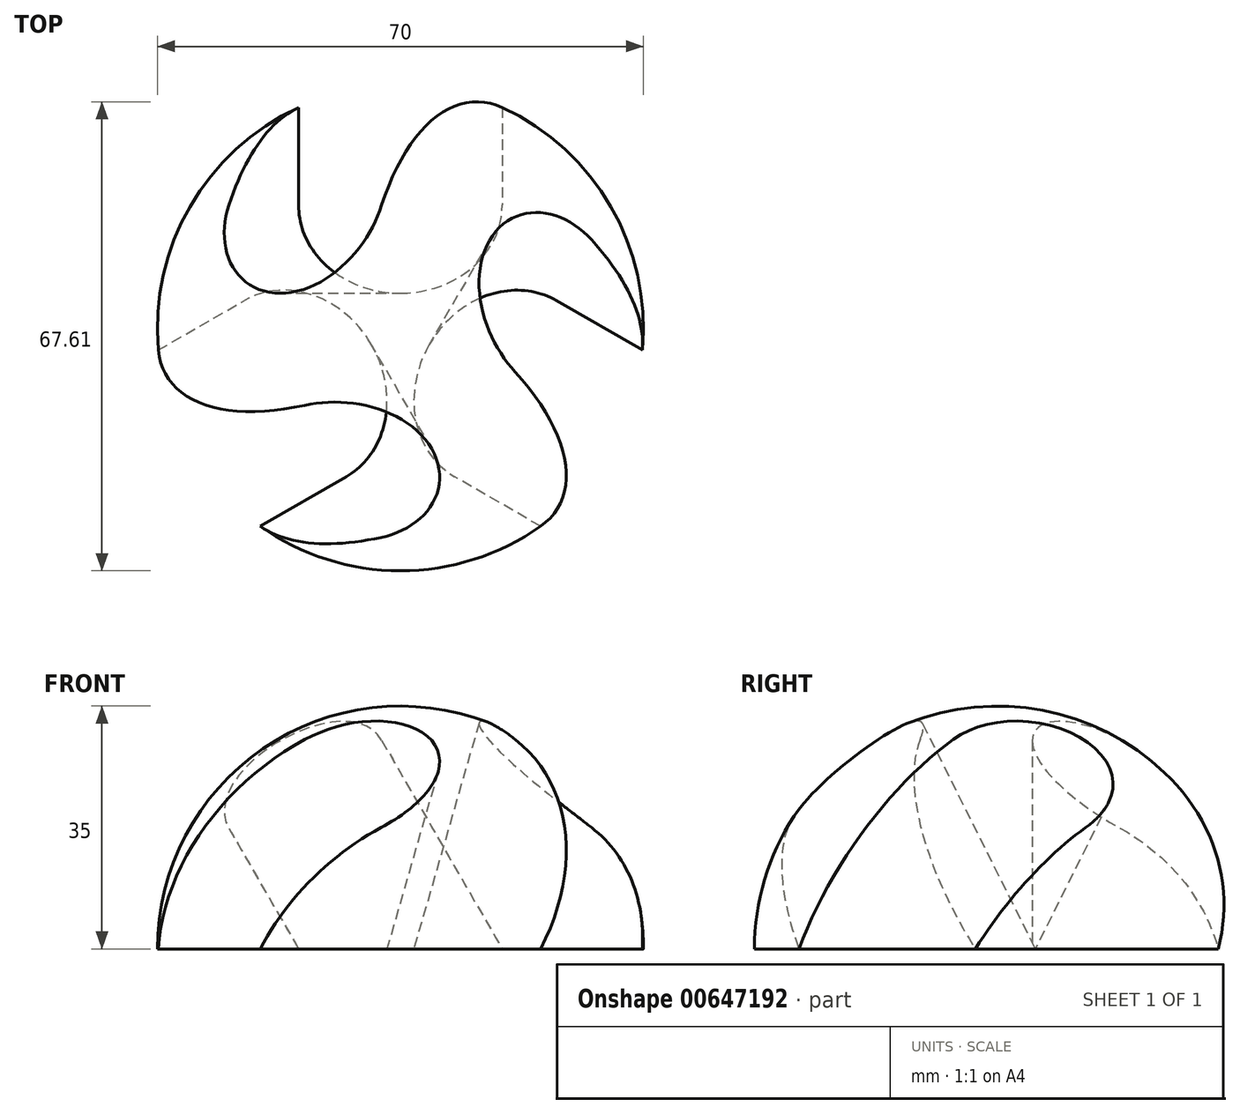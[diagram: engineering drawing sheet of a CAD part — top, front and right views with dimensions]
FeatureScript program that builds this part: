
annotation { "Feature Type Name" : "Feature", "Feature Type Description" : "" }
export const myFeature = defineFeature(function(context is Context, id is Id, definition is map)
    precondition{}
    {
        {
            var Q0;
            Q0=qCreatedBy(makeId("Top.planeOp"),FACE);
            var sketch = newSketch(context, id + "F0", { "sketchPlane" : qUnion([Q0])});
            skArc(sketch, "E0", {"start": v(0, -35) * mm, "mid": v(35, 0) * mm, "end": v(0, 35) * mm});
            skLineSegment(sketch, "E1", {"start": v(0, 35) * mm, "end": v(0, -35) * mm});
            skSolve(sketch);
        }
        {
            var Q0;
            Q0=qCreatedBy(makeId("Top.planeOp"),FACE);
            var sketch = newSketch(context, id + "F1", { "sketchPlane" : qUnion([Q0])});
            skLineSegment(sketch, "E2", {"start": v(0, 18.5) * mm, "end": v(0, -17.36) * mm, "construction": true});
            skSolve(sketch);
        }
        {
            var Q0;
            Q0 = qSketchRegion(id + "F0", true);
            var Q1;
            Q1=sQuery(id+"F0.wireOp",EDGE,"E1");
            revolve(context, id + "F2", {"entities" : qUnion([Q0]), "axis" : qUnion([Q1]), "revolveType" : RevolveType.FULL});
        }
        {
            var Q0;
            Q0=qCreatedBy(makeId("Front.planeOp"),FACE);
            var sketch = newSketch(context, id + "F3", { "sketchPlane" : qUnion([Q0])});
            skLineSegment(sketch, "E3.bottom", {"start": v(56.38, 0) * mm, "end": v(-54.62, 0) * mm});
            skLineSegment(sketch, "E3.top", {"start": v(56.38, -44.46) * mm, "end": v(-54.62, -44.46) * mm});
            skLineSegment(sketch, "E3.left", {"start": v(56.38, 0) * mm, "end": v(56.38, -44.46) * mm});
            skLineSegment(sketch, "E3.right", {"start": v(-54.62, 0) * mm, "end": v(-54.62, -44.46) * mm});
            skSolve(sketch);
        }
        {
            var Q0;
            Q0 = qSketchRegion(id + "F3", true);
            extrude(context, id + "F4", {"entities" : qUnion([Q0]), "operationType" : NewBodyOperationType.REMOVE, "oppositeDirection" : true, "depth" : 40 * mm, "offsetDistance" : 25 * mm, "hasSecondDirection" : true, "secondDirectionOppositeDirection" : false, "secondDirectionDepth" : 40 * mm});
        }
        {
            var Q0;
            Q0=qCreatedBy(makeId("Top.planeOp"),FACE);
            var Q1;
            Q1=sQuery(id+"F1.wireOp",EDGE,"E2");
            cPlane(context, id + "F5", {"entities" : qUnion([Q0, Q1]), "cplaneType" : CPlaneType.LINE_ANGLE, "offset" : 25 * mm, "angle" : 30 * degree, "width" : 150 * mm, "height" : 150 * mm});
        }
        {
            var Q0;
            Q0=qCreatedBy(id+"F5.planeOp",FACE);
            var sketch = newSketch(context, id + "F6", { "sketchPlane" : qUnion([Q0])});
            skArc(sketch, "E4", {"start": v(12.7, -17.72) * mm, "mid": v(0, -5.02) * mm, "end": v(-12.7, -17.72) * mm});
            skLineSegment(sketch, "E5.0", {"start": v(-12.7, -17.72) * mm, "end": v(-12.7, -40.82) * mm});
            skLineSegment(sketch, "E6.0", {"start": v(12.7, -17.72) * mm, "end": v(12.7, -40.82) * mm});
            skLineSegment(sketch, "E7.0", {"start": v(12.7, -40.82) * mm, "end": v(-12.7, -40.82) * mm});
            skSolve(sketch);
        }
        {
            var Q0;
            Q0 = qSketchRegion(id + "F6", true);
            extrude(context, id + "F7", {"entities" : qUnion([Q0]), "operationType" : NewBodyOperationType.REMOVE, "oppositeDirection" : true, "depth" : 60 * mm, "offsetDistance" : 25 * mm, "hasSecondDirection" : true, "secondDirectionOppositeDirection" : false, "secondDirectionDepth" : 25 * mm});
        }
        {
            var Q0;
            Q0=qCreatedBy(makeId("Top.planeOp"),FACE);
            var sketch = newSketch(context, id + "F8", { "sketchPlane" : qUnion([Q0])});
            skLineSegment(sketch, "E8", {"start": v(0, 0) * mm, "end": v(0, 44.27) * mm});
            skLineSegment(sketch, "E9", {"start": v(0, 0) * mm, "end": v(-30.31, -17.5) * mm});
            skLineSegment(sketch, "E10", {"start": v(0, 0) * mm, "end": v(30.31, -17.5) * mm});
            skArc(sketch, "E11.0", {"start": v(-14.66, 31.78) * mm, "mid": v(0, -35) * mm, "end": v(14.66, 31.78) * mm});
            skSolve(sketch);
        }
        {
            var Q0;
            Q0=qCreatedBy(makeId("Top.planeOp"),FACE);
            var sketch = newSketch(context, id + "F9", { "sketchPlane" : qUnion([Q0])});
            skLineSegment(sketch, "E12", {"start": v(0, 0) * mm, "end": v(-65.85, -38.02) * mm, "construction": true});
            skSolve(sketch);
        }
        {
            var Q0;
            Q0=qCreatedBy(makeId("Top.planeOp"),FACE);
            var Q1;
            Q1=sQuery(id+"F9.wireOp",EDGE,"E12");
            cPlane(context, id + "F10", {"entities" : qUnion([Q0, Q1]), "cplaneType" : CPlaneType.LINE_ANGLE, "offset" : 25 * mm, "angle" : 30 * degree, "oppositeDirection" : true, "width" : 150 * mm, "height" : 150 * mm});
        }
        {
            var Q0;
            Q0=qCreatedBy(id+"F10.planeOp",FACE);
            var sketch = newSketch(context, id + "F11", { "sketchPlane" : qUnion([Q0])});
            skArc(sketch, "E13", {"start": v(-21.33, -3.53) * mm, "mid": v(-4.3, 2.15) * mm, "end": v(-9.97, 19.19) * mm});
            skLineSegment(sketch, "E14.0", {"start": v(-9.97, 19.19) * mm, "end": v(-25.63, 27.01) * mm});
            skLineSegment(sketch, "E15.0", {"start": v(-21.33, -3.53) * mm, "end": v(-36.98, 4.3) * mm});
            skLineSegment(sketch, "E16", {"start": v(-25.63, 27.01) * mm, "end": v(-36.98, 4.3) * mm});
            skSolve(sketch);
        }
        {
            var Q0;
            Q0 = qSketchRegion(id + "F11", true);
            extrude(context, id + "F12", {"entities" : qUnion([Q0]), "operationType" : NewBodyOperationType.REMOVE, "oppositeDirection" : true, "depth" : 60 * mm, "offsetDistance" : 25 * mm, "hasSecondDirection" : true, "secondDirectionOppositeDirection" : false, "secondDirectionDepth" : 60 * mm});
        }
        {
            var Q0;
            Q0=qCreatedBy(makeId("Top.planeOp"),FACE);
            var sketch = newSketch(context, id + "F13", { "sketchPlane" : qUnion([Q0])});
            skLineSegment(sketch, "E17", {"start": v(0, 0) * mm, "end": v(53.93, -31.14) * mm, "construction": true});
            skSolve(sketch);
        }
        {
            var Q0;
            Q0=qCreatedBy(makeId("Top.planeOp"),FACE);
            var Q1;
            Q1=sQuery(id+"F13.wireOp",EDGE,"E17");
            cPlane(context, id + "F14", {"entities" : qUnion([Q0, Q1]), "cplaneType" : CPlaneType.LINE_ANGLE, "offset" : 25 * mm, "angle" : 30 * degree, "oppositeDirection" : true, "width" : 150 * mm, "height" : 150 * mm});
        }
        {
            var Q0;
            Q0=qCreatedBy(id+"F14.planeOp",FACE);
            var sketch = newSketch(context, id + "F15", { "sketchPlane" : qUnion([Q0])});
            skArc(sketch, "E18", {"start": v(9.97, 19.19) * mm, "mid": v(4.3, 2.15) * mm, "end": v(21.33, -3.53) * mm});
            skLineSegment(sketch, "E19.0", {"start": v(21.33, -3.53) * mm, "end": v(36.98, 4.3) * mm});
            skLineSegment(sketch, "E20.0", {"start": v(9.97, 19.19) * mm, "end": v(25.63, 27.01) * mm});
            skLineSegment(sketch, "E21", {"start": v(25.63, 27.01) * mm, "end": v(36.98, 4.3) * mm});
            skSolve(sketch);
        }
        {
            var Q0;
            Q0 = qSketchRegion(id + "F15", true);
            extrude(context, id + "F16", {"entities" : qUnion([Q0]), "operationType" : NewBodyOperationType.REMOVE, "oppositeDirection" : true, "depth" : 60 * mm, "offsetDistance" : 25 * mm, "hasSecondDirection" : true, "secondDirectionOppositeDirection" : false, "secondDirectionDepth" : 60 * mm});
        }
    });
